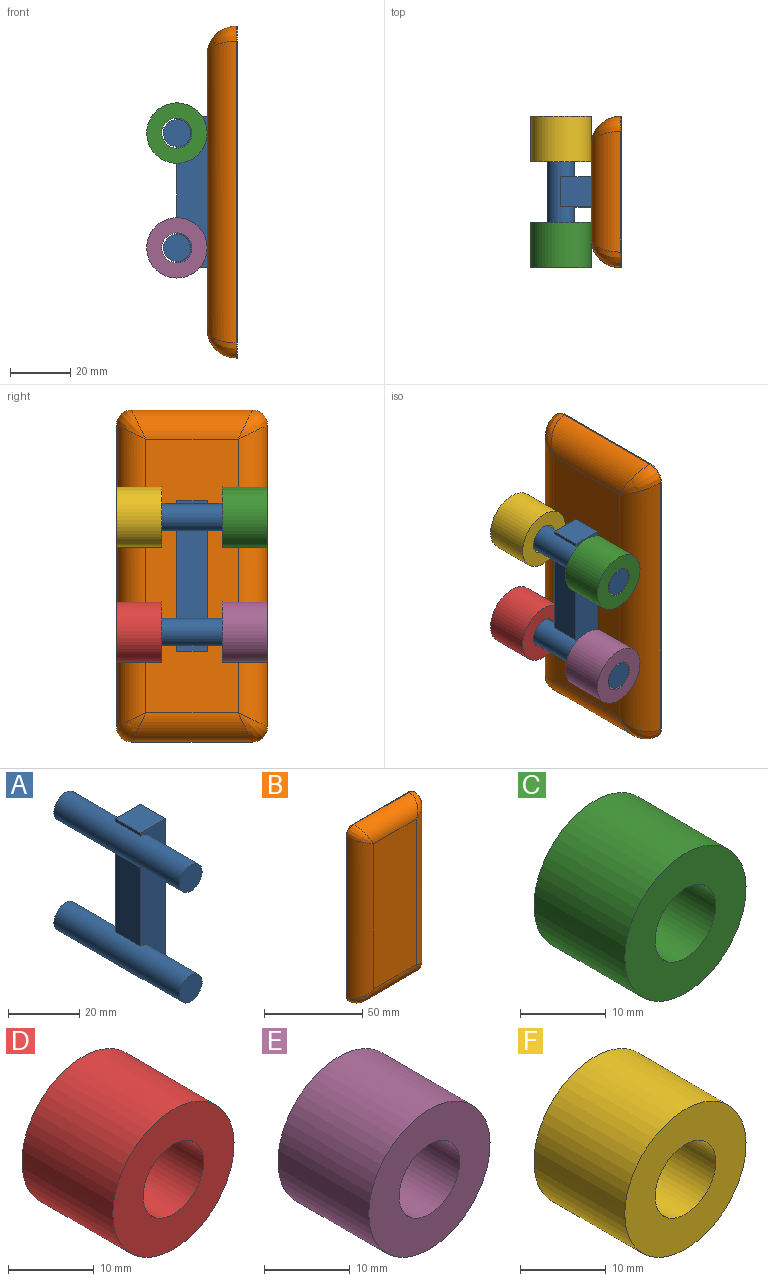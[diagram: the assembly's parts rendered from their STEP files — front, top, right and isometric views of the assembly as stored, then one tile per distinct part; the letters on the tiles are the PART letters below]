
ASSEMBLY  parts=6 mates=5
PART A: 14 faces, bbox 14.5x50x50 mm
  f0: plane 29.03x10mm, normal (-1,0,0), area 290.3mm2, adj f5,f6,f7,f9
  f1: plane 10x1.99mm, normal (-1,0,0), area 19.9mm2, adj f2,f5,f6,f9
  f2: plane 10x10mm, normal (0,0,-1), area 100mm2, adj f1,f5,f6,f13
  f3: plane 10x10mm, normal (0,0,1), area 100mm2, adj f4,f5,f6,f13
  f4: plane 10x0.98mm, normal (-1,0,0), area 9.8mm2, adj f3,f5,f6,f7
  f5: plane 50x10mm, normal (0,-1,0), area 436.4mm2, adj f0,f1,f2,f3,f4,f7,f9,f13
  f6: plane 50x10mm, normal (0,1,0), area 436.4mm2, adj f0,f1,f2,f3,f4,f7,f9,f13
  f7: cylinder r=4.5mm len=50mm, axis (0,1,0), area 1272.3mm2, adj f0,f4,f5,f6,f8,f11
  f8: plane 9x9mm, normal (0,-1,0), area 63.6mm2, adj f7
  f9: cylinder r=4.5mm len=50mm, axis (0,1,0), area 1272.3mm2, adj f0,f1,f5,f6,f10,f12
  f10: plane 9x9mm, normal (0,-1,0), area 63.6mm2, adj f9
  f11: plane 9x9mm, normal (0,1,0), area 63.6mm2, adj f7
  f12: plane 9x9mm, normal (0,1,0), area 63.6mm2, adj f9
  f13: plane 50x10mm, normal (1,0,0), area 500mm2, adj f2,f3,f5,f6
PART B: 18 faces, bbox 50x11.6x110 mm
  f0: plane 40x0.34mm, normal (0,0,1), area 13.7mm2, adj f1,f7,f9,f13
  f1: cylinder r=5mm len=5mm, axis (0,1,0), area 2.7mm2, adj f0,f2,f9,f11
  f2: plane 100x0.34mm, normal (-1,0,0), area 34.3mm2, adj f1,f3,f9,f10
  f3: cylinder r=5mm len=5mm, axis (0,1,0), area 2.7mm2, adj f2,f4,f9,f12
  f4: plane 40x0.34mm, normal (0,0,-1), area 13.7mm2, adj f3,f5,f9,f14
  f5: cylinder r=5mm len=5mm, axis (0,1,0), area 2.7mm2, adj f4,f6,f9,f16
  f6: plane 100x0.34mm, normal (1,0,0), area 34.3mm2, adj f5,f7,f9,f17
  f7: cylinder r=5mm len=5mm, axis (0,1,0), area 2.7mm2, adj f0,f6,f9,f15
  f8: plane 90.69x30.69mm, normal (0,-1,0), area 2782.8mm2, adj f10,f13,f14,f17
  f9: plane 110x50mm, normal (0,1,0), area 5478.5mm2, adj f0,f1,f2,f3,f4,f5,f6,f7
  f10: cylinder r=9.66mm len=100mm, axis (0,0,1), area 1465.6mm2, adj f2,f8,f11,f12
  f11: bspline ~11.55x9.66mm, area 79.5mm2, adj f1,f10,f13
  f12: bspline ~11.55x9.66mm, area 79.5mm2, adj f3,f10,f14
  f13: cylinder r=9.66mm len=40mm, axis (1,0,0), area 555.4mm2, adj f0,f8,f11,f15
  f14: cylinder r=9.66mm len=40mm, axis (-1,0,0), area 555.4mm2, adj f4,f8,f12,f16
  f15: bspline ~11.55x9.66mm, area 79.5mm2, adj f7,f13,f17
  f16: bspline ~11.55x9.66mm, area 79.5mm2, adj f5,f14,f17
  f17: cylinder r=9.66mm len=100mm, axis (0,0,-1), area 1465.6mm2, adj f6,f8,f15,f16
PART C: 4 faces, bbox 20x15x20 mm
  f0: cylinder r=5mm len=15mm, axis (0,1,0), area 471.2mm2, adj f2,f3
  f1: cylinder r=10mm len=20mm, axis (0,1,0), area 942.5mm2, adj f2,f3
  f2: plane 20x20mm, normal (0,-1,0), area 235.6mm2, adj f0,f1
  f3: plane 20x20mm, normal (0,1,0), area 235.6mm2, adj f0,f1
PART D: 4 faces, bbox 20x15x20 mm
  f0: cylinder r=5mm len=15mm, axis (0,1,0), area 471.2mm2, adj f2,f3
  f1: cylinder r=10mm len=20mm, axis (0,1,0), area 942.5mm2, adj f2,f3
  f2: plane 20x20mm, normal (0,-1,0), area 235.6mm2, adj f0,f1
  f3: plane 20x20mm, normal (0,1,0), area 235.6mm2, adj f0,f1
PART E: 4 faces, bbox 20x15x20 mm
  f0: cylinder r=5mm len=15mm, axis (0,1,0), area 471.2mm2, adj f2,f3
  f1: cylinder r=10mm len=20mm, axis (0,1,0), area 942.5mm2, adj f2,f3
  f2: plane 20x20mm, normal (0,-1,0), area 235.6mm2, adj f0,f1
  f3: plane 20x20mm, normal (0,1,0), area 235.6mm2, adj f0,f1
PART F: 4 faces, bbox 20x15x20 mm
  f0: cylinder r=5mm len=15mm, axis (0,1,0), area 471.2mm2, adj f2,f3
  f1: cylinder r=10mm len=20mm, axis (0,1,0), area 942.5mm2, adj f2,f3
  f2: plane 20x20mm, normal (0,-1,0), area 235.6mm2, adj f0,f1
  f3: plane 20x20mm, normal (0,1,0), area 235.6mm2, adj f0,f1
PLACE A t=(-66.01,-19.32,-44.92)mm
PLACE B rot(axis=(0,0,-1),90deg) t=(-51.01,-22.69,-29.31)mm
PLACE C t=(-53.98,-34.32,-10.4)mm
PLACE D t=(-85.55,0.68,-47.14)mm
PLACE E t=(-76.02,-34.32,-68.16)mm
PLACE F t=(-47.01,0.68,-31.8)mm
MATE slider A.f9 <-> E.f0  axis (0,-1,0) through (-71.01,-49.32,-61.23)mm
MATE slider C.f0 <-> A.f7  axis (0,-1,0) through (-71.01,-49.32,-23.2)mm
MATE slider D.f0 <-> A.f9  axis (0,1,0) through (-71.01,0.68,-61.23)mm
MATE slider F.f0 <-> A.f7  axis (0,1,0) through (-71.01,0.68,-23.2)mm
MATE slider B.f8 <-> A.f13  axis (-1,0,0) through (-61.01,-24.32,-42.72)mm
